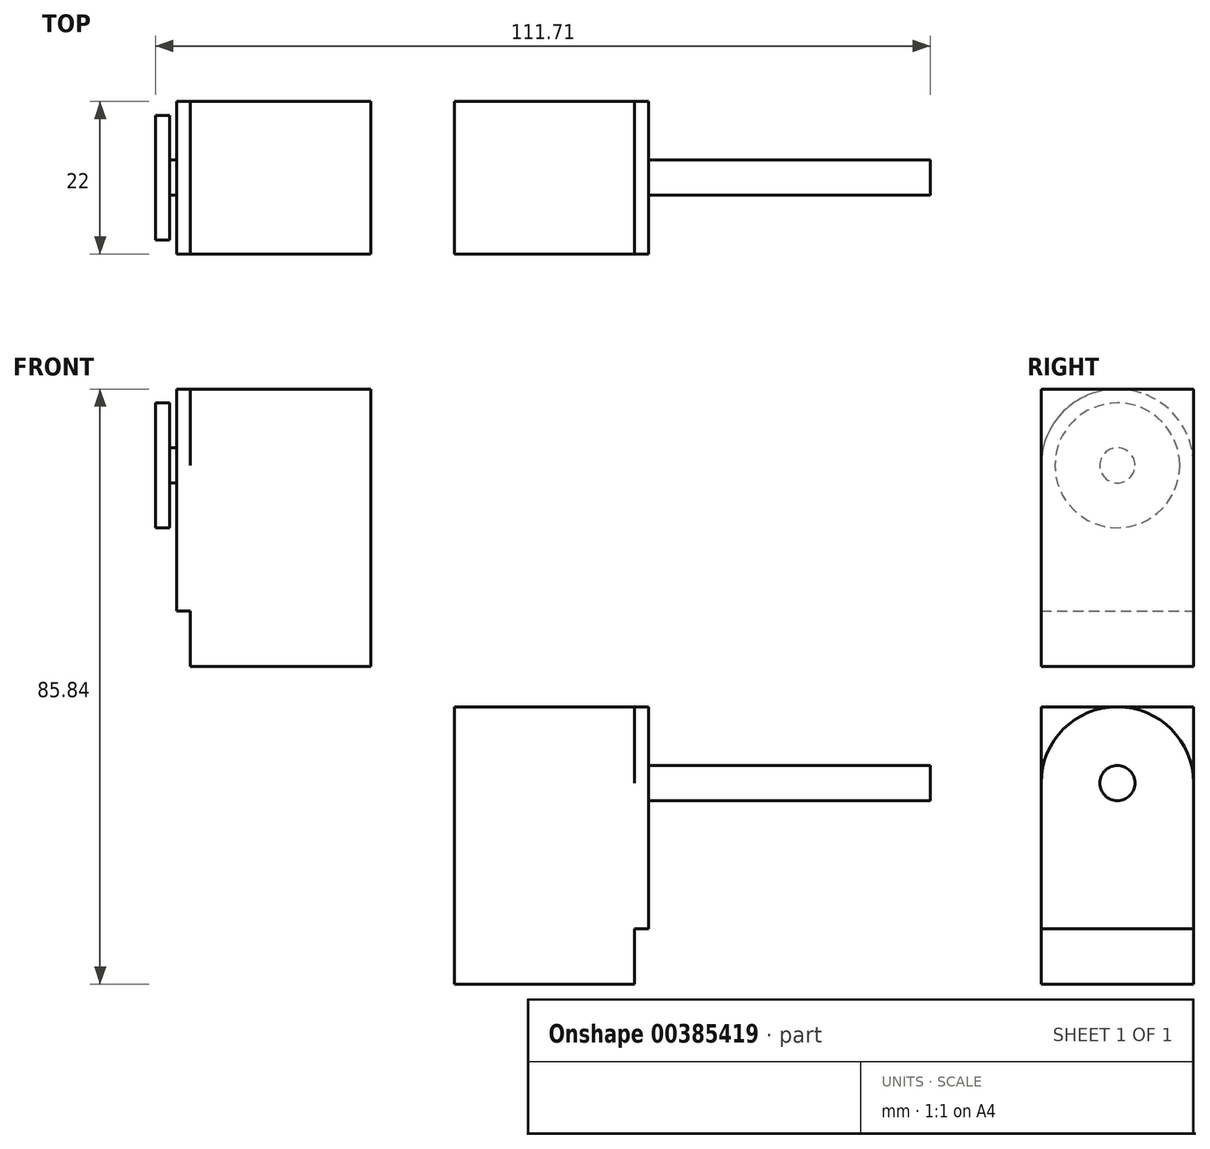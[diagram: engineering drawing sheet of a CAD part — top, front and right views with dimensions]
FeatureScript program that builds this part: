
annotation { "Feature Type Name" : "Feature", "Feature Type Description" : "" }
export const myFeature = defineFeature(function(context is Context, id is Id, definition is map)
    precondition{}
    {
        {
            var Q0;
            Q0=qCreatedBy(makeId("Front.planeOp"),FACE);
            var sketch = newSketch(context, id + "F0", { "sketchPlane" : qUnion([Q0])});
            skLineSegment(sketch, "E0", {"start": v(-15.28, 6.7) * mm, "end": v(10.72, 6.7) * mm});
            skLineSegment(sketch, "E1", {"start": v(10.72, 6.7) * mm, "end": v(10.72, -33.3) * mm});
            skLineSegment(sketch, "E2", {"start": v(10.72, -33.3) * mm, "end": v(-15.28, -33.3) * mm});
            skLineSegment(sketch, "E3", {"start": v(-15.28, -33.3) * mm, "end": v(-15.28, 6.7) * mm});
            skSolve(sketch);
        }
        {
            var Q0;
            Q0 = qSketchRegion(id + "F0", true);
            extrude(context, id + "F1", {"entities" : qUnion([Q0]), "depth" : 22 * mm});
        }
        {
            var Q0;
            Q0=makeQuery(id+"F1.opExtrude","SWEPT_FACE",FACE,{"disambiguationData":[OSD([sQuery(id+"F0.wireOp",EDGE,"E1")])]});
            var sketch = newSketch(context, id + "F2", { "sketchPlane" : qUnion([Q0])});
            skLineSegment(sketch, "E4", {"start": v(-22, -25.3) * mm, "end": v(0, -25.3) * mm});
            skLineSegment(sketch, "E5", {"start": v(0, -25.3) * mm, "end": v(0, -4.3) * mm});
            skLineSegment(sketch, "E6", {"start": v(-11, 6.7) * mm, "end": v(-11, 6.7) * mm});
            skLineSegment(sketch, "E7", {"start": v(-22, -4.3) * mm, "end": v(-22, -25.3) * mm});
            skPoint(sketch, "E8.visualSharp", {"position": v(0, 6.7) * mm});
            skArc(sketch, "E8.filletArc", {"start": v(0, -4.3) * mm, "mid": v(-3.22, 3.48) * mm, "end": v(-11, 6.7) * mm});
            skPoint(sketch, "E9.visualSharp", {"position": v(-22, 6.7) * mm});
            skArc(sketch, "E9.filletArc", {"start": v(-11, 6.7) * mm, "mid": v(-18.78, 3.48) * mm, "end": v(-22, -4.3) * mm});
            skSolve(sketch);
        }
        {
            var Q0;
            Q0=makeQuery(id+"F2.imprint","IMPRINT",FACE,{"disambiguationData":[TD([[makeQuery(id+"F2.imprint","IMPRINT",EDGE,{"derivedFrom":sQuery(id+"F2.wireOp",EDGE,"E4")}),1.0]])]});
            extrude(context, id + "F3", {"entities" : qUnion([Q0]), "operationType" : NewBodyOperationType.ADD, "depth" : 2 * mm});
        }
        {
            var Q0;
            Q0=makeQuery(id+"F3.opExtrude","CAP_FACE",FACE,{"disambiguationData":[OSD([sQuery(id+"F2.wireOp",EDGE,"E4"),sQuery(id+"F2.wireOp",EDGE,"E5"),sQuery(id+"F2.wireOp",EDGE,"E7"),sQuery(id+"F2.wireOp",EDGE,"E8.filletArc"),sQuery(id+"F2.wireOp",EDGE,"E9.filletArc")])],"isStart":false});
            var sketch = newSketch(context, id + "F4", { "sketchPlane" : qUnion([Q0])});
            skPoint(sketch, "E10", {"position": v(-11, -4.3) * mm});
            skCircle(sketch, "E11", {"center": v(-11, -4.3) * mm, "radius": 2.54 * mm});
            skSolve(sketch);
        }
        {
            var Q0;
            Q0=makeQuery(id+"F4.imprint","IMPRINT",FACE,{"disambiguationData":[TD([[makeQuery(id+"F4.imprint","IMPRINT",EDGE,{"derivedFrom":sQuery(id+"F4.wireOp",EDGE,"E11")}),1.0]])]});
            extrude(context, id + "F5", {"entities" : qUnion([Q0]), "operationType" : NewBodyOperationType.ADD, "depth" : 40.64 * mm});
        }
        {
            var Q0;
            Q0=qCreatedBy(makeId("Front.planeOp"),FACE);
            var sketch = newSketch(context, id + "F6", { "sketchPlane" : qUnion([Q0])});
            skLineSegment(sketch, "E12", {"start": v(-53.35, 52.54) * mm, "end": v(-27.35, 52.54) * mm});
            skLineSegment(sketch, "E13", {"start": v(-27.35, 52.54) * mm, "end": v(-27.35, 12.54) * mm});
            skLineSegment(sketch, "E14", {"start": v(-27.35, 12.54) * mm, "end": v(-53.35, 12.54) * mm});
            skLineSegment(sketch, "E15", {"start": v(-53.35, 12.54) * mm, "end": v(-53.35, 52.54) * mm});
            skSolve(sketch);
        }
        {
            var Q0;
            Q0=makeQuery(id+"F6.imprint","IMPRINT",FACE,{"disambiguationData":[TD([[makeQuery(id+"F6.imprint","IMPRINT",EDGE,{"derivedFrom":sQuery(id+"F6.wireOp",EDGE,"E12")}),-1.0]])]});
            extrude(context, id + "F7", {"entities" : qUnion([Q0]), "depth" : 22 * mm});
        }
        {
            var Q0;
            Q0=makeQuery(id+"F7.opExtrude","SWEPT_FACE",FACE,{"disambiguationData":[OSD([sQuery(id+"F6.wireOp",EDGE,"E15")])]});
            var sketch = newSketch(context, id + "F8", { "sketchPlane" : qUnion([Q0])});
            skLineSegment(sketch, "E16", {"start": v(0, 20.54) * mm, "end": v(0, 41.54) * mm});
            skLineSegment(sketch, "E17", {"start": v(11, 52.54) * mm, "end": v(11, 52.54) * mm});
            skLineSegment(sketch, "E18", {"start": v(22, 41.54) * mm, "end": v(22, 20.54) * mm});
            skLineSegment(sketch, "E19", {"start": v(22, 20.54) * mm, "end": v(0, 20.54) * mm});
            skPoint(sketch, "E20.visualSharp", {"position": v(0, 52.54) * mm});
            skArc(sketch, "E20.filletArc", {"start": v(11, 52.54) * mm, "mid": v(3.22, 49.32) * mm, "end": v(0, 41.54) * mm});
            skPoint(sketch, "E21.visualSharp", {"position": v(22, 52.54) * mm});
            skArc(sketch, "E21.filletArc", {"start": v(22, 41.54) * mm, "mid": v(18.78, 49.32) * mm, "end": v(11, 52.54) * mm});
            skCircle(sketch, "E22", {"center": v(11, 41.54) * mm, "radius": 2.54 * mm});
            skSolve(sketch);
        }
        {
            var Q0;
            Q0=makeQuery(id+"F8.imprint","IMPRINT",FACE,{"disambiguationData":[TD([[makeQuery(id+"F8.imprint","IMPRINT",EDGE,{"derivedFrom":sQuery(id+"F8.wireOp",EDGE,"E16")}),-1.0]])]});
            var Q1;
            Q1=makeQuery(id+"F8.imprint","IMPRINT",FACE,{"disambiguationData":[TD([[makeQuery(id+"F8.imprint","IMPRINT",EDGE,{"derivedFrom":sQuery(id+"F8.wireOp",EDGE,"E22")}),1.0]])]});
            extrude(context, id + "F9", {"entities" : qUnion([Q0, Q1]), "operationType" : NewBodyOperationType.ADD, "depth" : 2 * mm});
        }
        {
            var Q0;
            Q0=makeQuery(id+"F9.opExtrude","CAP_FACE",FACE,{"disambiguationData":[OSD([sQuery(id+"F8.wireOp",EDGE,"E16"),sQuery(id+"F8.wireOp",EDGE,"E18"),sQuery(id+"F8.wireOp",EDGE,"E19"),sQuery(id+"F8.wireOp",EDGE,"E20.filletArc"),sQuery(id+"F8.wireOp",EDGE,"E21.filletArc")])],"isStart":false});
            var sketch = newSketch(context, id + "F10", { "sketchPlane" : qUnion([Q0])});
            skCircle(sketch, "E23.0", {"center": v(11, 41.54) * mm, "radius": 2.54 * mm});
            skSolve(sketch);
        }
        {
            var Q0;
            Q0 = qSketchRegion(id + "F10", true);
            extrude(context, id + "F11", {"entities" : qUnion([Q0]), "operationType" : NewBodyOperationType.ADD, "depth" : 1 * mm});
        }
        {
            var Q0;
            Q0=makeQuery(id+"F11.opExtrude","CAP_FACE",FACE,{"disambiguationData":[OSD([sQuery(id+"F10.wireOp",EDGE,"E23.0")])],"isStart":false});
            var sketch = newSketch(context, id + "F12", { "sketchPlane" : qUnion([Q0])});
            skCircle(sketch, "E24", {"center": v(11, 41.54) * mm, "radius": 9 * mm});
            skSolve(sketch);
        }
        {
            var Q0;
            Q0=makeQuery(id+"F12.imprint","IMPRINT",FACE,{"disambiguationData":[TD([[makeQuery(id+"F12.imprint","IMPRINT",EDGE,{"derivedFrom":makeQuery(id+"F11.opExtrude","CAP_EDGE",EDGE,{"disambiguationData":[OSD([sQuery(id+"F10.wireOp",EDGE,"E23.0")])],"isStart":false})}),1.0]])]});
            var Q1;
            Q1=makeQuery(id+"F12.imprint","IMPRINT",FACE,{"disambiguationData":[TD([[makeQuery(id+"F12.imprint","IMPRINT",EDGE,{"derivedFrom":sQuery(id+"F12.wireOp",EDGE,"E24")}),1.0]])]});
            extrude(context, id + "F13", {"entities" : qUnion([Q0, Q1]), "operationType" : NewBodyOperationType.ADD, "depth" : 2 * mm});
        }
    });
